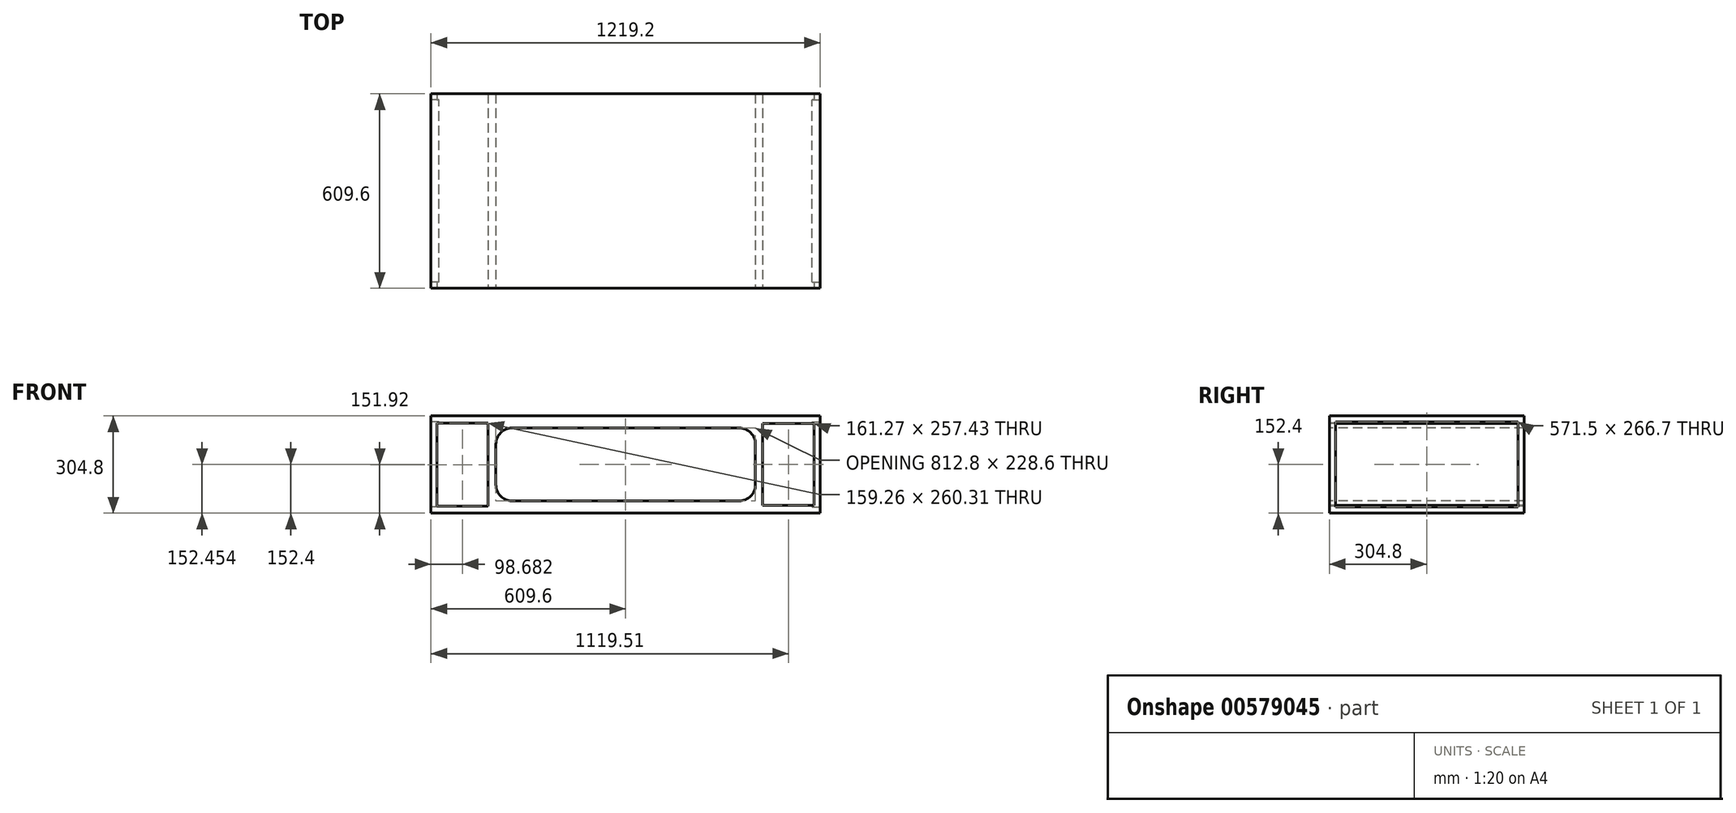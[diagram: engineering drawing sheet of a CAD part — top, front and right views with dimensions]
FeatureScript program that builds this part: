
annotation { "Feature Type Name" : "Feature", "Feature Type Description" : "" }
export const myFeature = defineFeature(function(context is Context, id is Id, definition is map)
    precondition{}
    {
        {
            var Q0;
            Q0=qCreatedBy(makeId("Top.planeOp"),FACE);
            var sketch = newSketch(context, id + "F0", { "sketchPlane" : qUnion([Q0])});
            skLineSegment(sketch, "E0.bottom", {"start": v(609.6, -304.8) * mm, "end": v(-609.6, -304.8) * mm});
            skLineSegment(sketch, "E0.top", {"start": v(609.6, 304.8) * mm, "end": v(-609.6, 304.8) * mm});
            skLineSegment(sketch, "E0.left", {"start": v(609.6, -304.8) * mm, "end": v(609.6, 304.8) * mm});
            skLineSegment(sketch, "E0.right", {"start": v(-609.6, -304.8) * mm, "end": v(-609.6, 304.8) * mm});
            skPoint(sketch, "E0.middle", {"position": v(0, 0) * mm});
            skSolve(sketch);
        }
        {
            var Q0;
            Q0=makeQuery(id+"F0.imprint","IMPRINT",FACE,{"disambiguationData":[TD([[makeQuery(id+"F0.imprint","IMPRINT",EDGE,{"derivedFrom":sQuery(id+"F0.wireOp",EDGE,"E0.bottom")}),-1.0]])]});
            extrude(context, id + "F1", {"entities" : qUnion([Q0]), "endBound" : BoundingType.SYMMETRIC, "depth" : 304.8 * mm, "offsetDistance" : 25.4 * mm});
        }
        {
            var Q0;
            Q0=makeQuery(id+"F1.opExtrude","SWEPT_FACE",FACE,{"disambiguationData":[OSD([sQuery(id+"F0.wireOp",EDGE,"E0.bottom")])]});
            var sketch = newSketch(context, id + "F2", { "sketchPlane" : qUnion([Q0])});
            skLineSegment(sketch, "E1.bottom", {"start": v(355.6, -114.3) * mm, "end": v(-355.6, -114.3) * mm});
            skLineSegment(sketch, "E1.top", {"start": v(355.6, 114.3) * mm, "end": v(-355.6, 114.3) * mm});
            skLineSegment(sketch, "E1.left", {"start": v(406.4, -63.5) * mm, "end": v(406.4, 63.5) * mm});
            skLineSegment(sketch, "E1.right", {"start": v(-406.4, -63.5) * mm, "end": v(-406.4, 63.5) * mm});
            skPoint(sketch, "E1.middle", {"position": v(0, 0) * mm});
            skPoint(sketch, "E2.visualSharp", {"position": v(-406.4, 114.3) * mm});
            skArc(sketch, "E2.filletArc", {"start": v(-355.6, 114.3) * mm, "mid": v(-391.52, 99.42) * mm, "end": v(-406.4, 63.5) * mm});
            skPoint(sketch, "E3.visualSharp", {"position": v(406.4, 114.3) * mm});
            skArc(sketch, "E3.filletArc", {"start": v(406.4, 63.5) * mm, "mid": v(391.52, 99.42) * mm, "end": v(355.6, 114.3) * mm});
            skPoint(sketch, "E4.visualSharp", {"position": v(406.4, -114.3) * mm});
            skArc(sketch, "E4.filletArc", {"start": v(355.6, -114.3) * mm, "mid": v(391.52, -99.42) * mm, "end": v(406.4, -63.5) * mm});
            skPoint(sketch, "E5.visualSharp", {"position": v(-406.4, -114.3) * mm});
            skArc(sketch, "E5.filletArc", {"start": v(-406.4, -63.5) * mm, "mid": v(-391.52, -99.42) * mm, "end": v(-355.6, -114.3) * mm});
            skSolve(sketch);
        }
        {
            var Q0;
            Q0=makeQuery(id+"F2.imprint","IMPRINT",FACE,{"disambiguationData":[TD([[makeQuery(id+"F2.imprint","IMPRINT",EDGE,{"derivedFrom":sQuery(id+"F2.wireOp",EDGE,"E1.bottom")}),-1.0]])]});
            extrude(context, id + "F3", {"entities" : qUnion([Q0]), "operationType" : NewBodyOperationType.REMOVE, "oppositeDirection" : true, "depth" : 1219.2 * mm, "offsetDistance" : 25.4 * mm});
        }
        {
            var Q0;
            Q0=makeQuery(id+"F1.opExtrude","SWEPT_FACE",FACE,{"disambiguationData":[OSD([sQuery(id+"F0.wireOp",EDGE,"E0.bottom")])]});
            var sketch = newSketch(context, id + "F4", { "sketchPlane" : qUnion([Q0])});
            skLineSegment(sketch, "E6", {"start": v(590.55, 128.77) * mm, "end": v(429.28, 128.77) * mm});
            skLineSegment(sketch, "E7", {"start": v(429.28, 128.77) * mm, "end": v(429.28, -128.66) * mm});
            skLineSegment(sketch, "E8", {"start": v(429.28, -128.66) * mm, "end": v(590.55, -128.66) * mm});
            skLineSegment(sketch, "E9", {"start": v(-590.55, 129.67) * mm, "end": v(-431.29, 129.67) * mm});
            skLineSegment(sketch, "E10", {"start": v(-431.29, 129.67) * mm, "end": v(-431.29, -130.63) * mm});
            skLineSegment(sketch, "E11", {"start": v(-431.29, -130.63) * mm, "end": v(-590.55, -130.63) * mm});
            skLineSegment(sketch, "E12.0", {"start": v(590.55, -128.66) * mm, "end": v(590.55, 128.77) * mm});
            skLineSegment(sketch, "E13.0", {"start": v(-590.55, -130.63) * mm, "end": v(-590.55, 129.67) * mm});
            skPoint(sketch, "E14.orphan", {"position": v(-609.6, -130.63) * mm});
            skPoint(sketch, "E15.orphan", {"position": v(609.6, -128.66) * mm});
            skSolve(sketch);
        }
        {
            var Q0;
            Q0 = qSketchRegion(id + "F4", true);
            extrude(context, id + "F5", {"entities" : qUnion([Q0]), "operationType" : NewBodyOperationType.REMOVE, "oppositeDirection" : true, "depth" : 1219.2 * mm, "offsetDistance" : 25.4 * mm});
        }
        {
            var Q0;
            Q0=makeQuery(id+"F1.opExtrude","SWEPT_FACE",FACE,{"disambiguationData":[OSD([sQuery(id+"F0.wireOp",EDGE,"E0.left")])]});
            var sketch = newSketch(context, id + "F6", { "sketchPlane" : qUnion([Q0])});
            skLineSegment(sketch, "E16.0", {"start": v(-285.75, -133.35) * mm, "end": v(285.75, -133.35) * mm});
            skLineSegment(sketch, "E16.1", {"start": v(-285.75, 133.35) * mm, "end": v(-285.75, -133.35) * mm});
            skLineSegment(sketch, "E16.2", {"start": v(285.75, 133.35) * mm, "end": v(-285.75, 133.35) * mm});
            skLineSegment(sketch, "E16.3", {"start": v(285.75, -133.35) * mm, "end": v(285.75, 133.35) * mm});
            skSolve(sketch);
        }
        {
            var Q0;
            Q0 = qSketchRegion(id + "F6", true);
            extrude(context, id + "F7", {"entities" : qUnion([Q0]), "operationType" : NewBodyOperationType.REMOVE, "oppositeDirection" : true, "depth" : 25.4 * mm, "offsetDistance" : 25.4 * mm});
        }
        {
            var Q0;
            Q0=makeQuery(id+"F1.opExtrude","SWEPT_FACE",FACE,{"disambiguationData":[OSD([sQuery(id+"F0.wireOp",EDGE,"E0.right")])]});
            var sketch = newSketch(context, id + "F8", { "sketchPlane" : qUnion([Q0])});
            skLineSegment(sketch, "E17.0.0", {"start": v(-304.8, -152.4) * mm, "end": v(304.8, -152.4) * mm});
            skLineSegment(sketch, "E17.0.1", {"start": v(304.8, -152.4) * mm, "end": v(304.8, 152.4) * mm});
            skLineSegment(sketch, "E17.0.2", {"start": v(304.8, 152.4) * mm, "end": v(-304.8, 152.4) * mm});
            skLineSegment(sketch, "E17.0.3", {"start": v(-304.8, 152.4) * mm, "end": v(-304.8, -152.4) * mm});
            skLineSegment(sketch, "E18.0", {"start": v(-285.75, -133.35) * mm, "end": v(285.75, -133.35) * mm});
            skLineSegment(sketch, "E18.1", {"start": v(-285.75, 133.35) * mm, "end": v(-285.75, -133.35) * mm});
            skLineSegment(sketch, "E18.2", {"start": v(285.75, 133.35) * mm, "end": v(-285.75, 133.35) * mm});
            skLineSegment(sketch, "E18.3", {"start": v(285.75, -133.35) * mm, "end": v(285.75, 133.35) * mm});
            skSolve(sketch);
        }
        {
            var Q0;
            Q0=makeQuery(id+"F8.imprint","IMPRINT",FACE,{"disambiguationData":[TD([[makeQuery(id+"F8.imprint","IMPRINT",EDGE,{"derivedFrom":sQuery(id+"F8.wireOp",EDGE,"E18.0")}),1.0]])]});
            extrude(context, id + "F9", {"entities" : qUnion([Q0]), "operationType" : NewBodyOperationType.REMOVE, "oppositeDirection" : true, "depth" : 25.4 * mm, "offsetDistance" : 25.4 * mm});
        }
    });
